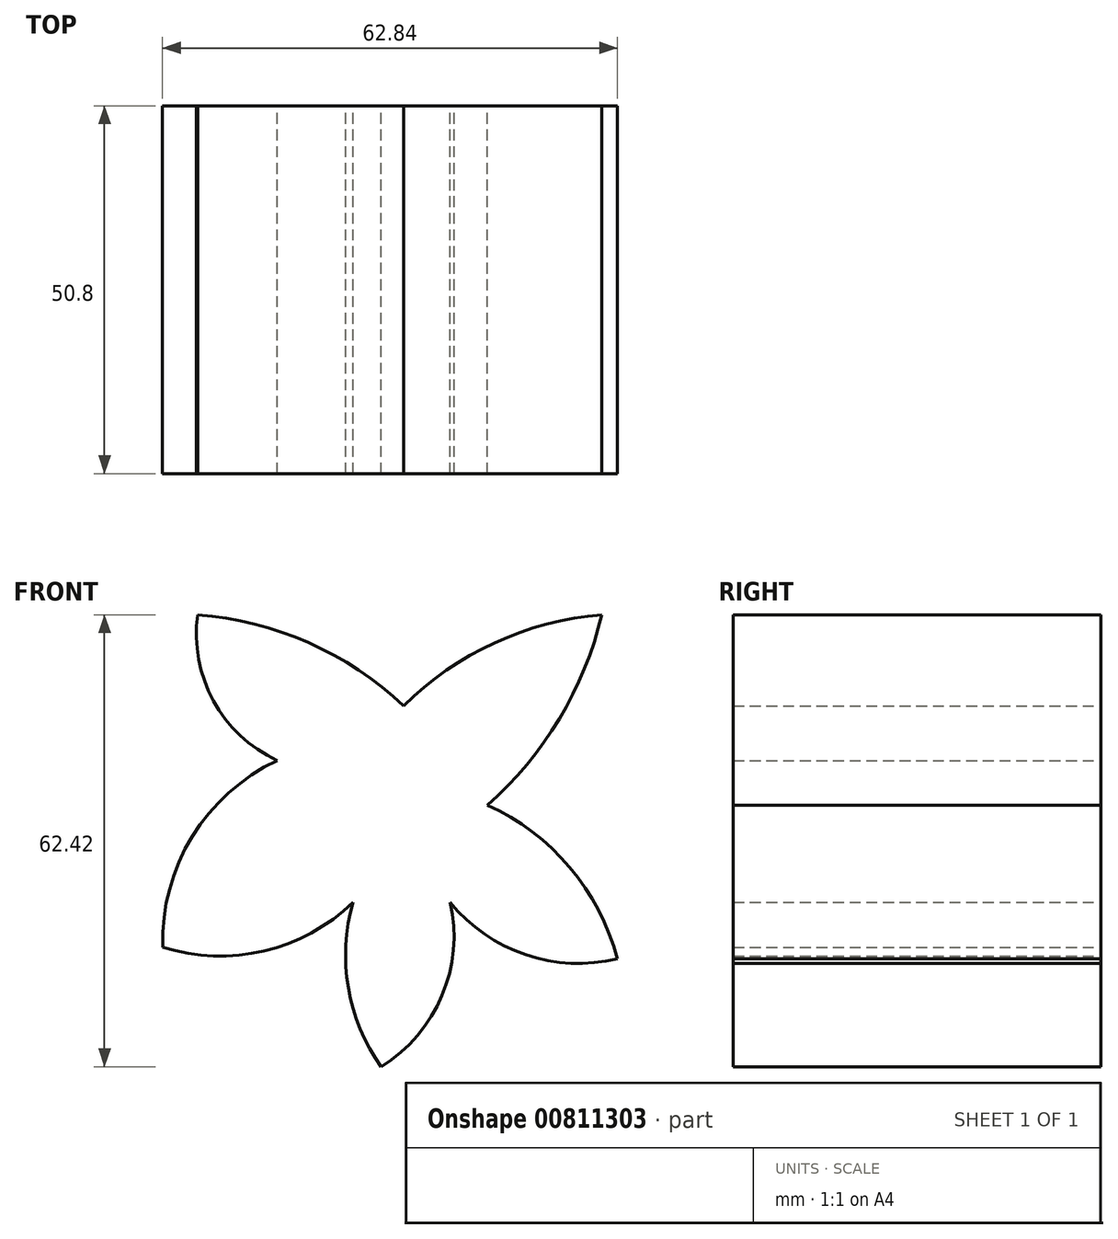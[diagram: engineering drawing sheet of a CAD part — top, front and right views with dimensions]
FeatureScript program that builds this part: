
annotation { "Feature Type Name" : "Feature", "Feature Type Description" : "" }
export const myFeature = defineFeature(function(context is Context, id is Id, definition is map)
    precondition{}
    {
        {
            var Q0;
            Q0=qCreatedBy(makeId("Front.planeOp"),FACE);
            var sketch = newSketch(context, id + "F0", { "sketchPlane" : qUnion([Q0])});
            skArc(sketch, "E0", {"start": v(30.47, 62.42) * mm, "mid": v(15.66, 58.55) * mm, "end": v(3.09, 49.8) * mm});
            skArc(sketch, "E1", {"start": v(3.09, 49.8) * mm, "mid": v(-10.06, 58.56) * mm, "end": v(-25.37, 62.42) * mm});
            skArc(sketch, "E2", {"start": v(14.63, 36.11) * mm, "mid": v(24.6, 48.04) * mm, "end": v(30.47, 62.42) * mm});
            skArc(sketch, "E3", {"start": v(32.62, 14.9) * mm, "mid": v(26.03, 27.54) * mm, "end": v(14.63, 36.11) * mm});
            skArc(sketch, "E4", {"start": v(9.53, 22.69) * mm, "mid": v(19.95, 15.46) * mm, "end": v(32.62, 14.9) * mm});
            skArc(sketch, "E5", {"start": v(0, 0) * mm, "mid": v(8.39, 9.82) * mm, "end": v(9.53, 22.69) * mm});
            skArc(sketch, "E6", {"start": v(-3.9, 22.69) * mm, "mid": v(-4.56, 10.9) * mm, "end": v(0, 0) * mm});
            skArc(sketch, "E7", {"start": v(-30.2, 16.51) * mm, "mid": v(-16.2, 16) * mm, "end": v(-3.9, 22.69) * mm});
            skArc(sketch, "E8", {"start": v(-14.36, 42.29) * mm, "mid": v(-26.13, 31.76) * mm, "end": v(-30.2, 16.51) * mm});
            skArc(sketch, "E9", {"start": v(-25.37, 62.42) * mm, "mid": v(-23.2, 50.54) * mm, "end": v(-14.36, 42.29) * mm});
            skSolve(sketch);
        }
        {
            var Q0;
            Q0=makeQuery(id+"F0.imprint","IMPRINT",FACE,{"disambiguationData":[TD([[makeQuery(id+"F0.imprint","IMPRINT",EDGE,{"derivedFrom":sQuery(id+"F0.wireOp",EDGE,"E0")}),1.0]])]});
            extrude(context, id + "F1", {"entities" : qUnion([Q0]), "depth" : 50.8 * mm, "offsetDistance" : 25.4 * mm});
        }
    });
